# Revit family: PRD_AR_JntrlUnits_SiriusMultiPurposeSink_LTJ450,LTJ500
name_source: partatom
category: Plumbing Fixtures
revit_build: Autodesk Revit 2018 (Build: 20190510_1515(x64)
units: mm (PartAtom-declared; Revit-internal decimal feet)

## family parameters
Cut with Voids When Loaded = No
Host = Face
OmniClass Number = 23.45.05.14.14
OmniClass Title = Sinks/Lavatories
Part Type = Normal
Room Calculation Point = No
Round Connector Dimension = Use Diameter
Shared = No

## types (2) — shared parameters
AssetType = Fixed
Category = Pr_40_20_96_44, Janitorial sinks
Color = Stainless steel
Default Elevation = 850 mm  [stored 2.78871 ft]
DrainSize = DN 40 (1 1/2 inch.)
DurationUnit = year
Finish = Satin finished
FinishAndMaterial = Stainless steel 1.4301
Form = Stainless steel multi purpose sink
IfcExportAs = IfcSanitaryTerminalType
IfcExportType = SINK
IntegralAccessories = incl. stainless steel screws and dowels
Manufacturer = KWC Group AG
ManufacturerName = KWC Group AG
ManufacturerURL = www.kwc.com
Material = Stainless steel
NBSDescription = Janitorial units
NBSReference = 45-35-70/401
NominalHeight = 270 mm  [stored 0.885827 ft]
OutletSize = DN 40 (1 1/2 inch.)
ProductInformation = https://pim.kwc.com
Shape = Rectangular
SinkMaterial = PRD_AR_StainlessSteel_SatinFinished
SinkMounting = WallHung
SinkType = Other
URL = www.kwc.com
Uniclass2015Code = Pr_40_20_96_44
Uniclass2015Title = Janitorial sinks
Uniclass2015Version = Products v1.10
Version = 1
WarrantyDurationUnit = year
WasteSize = 40  [stored 0.131234 ft]
WaterSupplyOverflowAndWasteHolesOverflow = Yes
WaterSupplyOverflowAndWasteHolesWaste = Center-Center
WaterSupplyOverflowAndWasteHolesWaterSupply = No tapholes

## per-type parameters (varying)
| type | BIMObjectName | Description | Features | GrossWeight | HingedGrateZSIRX001 | ModelNumber | Name | NetWeight | NominalDepth | NominalWidth | Size |
| LTJ450 | PRD_AR_JanitorialUnits_SiriusMultiPurposeSink_LTJ450 | General purpose utility sink for wall mounting, stainless steel, surface satin finished, material thickness 0.9 mm, front panel with riffle, 1 1/2 centric plug waste, with overflow, 30 mm rear upstand, prewelded mounting brackets, incl. stainless steel screws and dowels. Optinally available hinged grid Z-SIRX001: loosely attached - for side mount. | stainless steel, 0.90 mm, satin finished, wall mounting, 470x270x430 mm (WxHxD) | 5.10 kg | Yes | 2000057085 | Sirius multi purpose sink LTJ450 | 4.40 kg | 430 mm  [stored 1.41076 ft] | 470 mm  [stored 1.54199 ft] | 470 x 430 x 270 mm |
| LTJ500 | PRD_AR_JanitorialUnits_SiriusMultiPurposeSink_LTJ500 | General purpose utility sink for wall mounting, stainless steel, surface satin finished, material thickness 0.9 mm, front panel with riffle, 1 1/2 centric plug waste, with overflow, 30 mm rear upstand, prewelded mounting brackets, incl. stainless steel screws and dowels. | stainless steel, 0.90 mm, satin finished, wall mounting, 520x270x490 mm (WxHxD) | 5.60 kg | No | 2000057087 | Sirius multi purpose sink LTJ500 | 4.90 kg | 490 mm  [stored 1.60761 ft] | 520 mm  [stored 1.70604 ft] | 520 x 490 x 270 mm |

note: column(s) folded — value = type name in every type: Model, ModelReference, TypeOfSink

note: [stored X ft] marks values corroborated as IEEE doubles in the binary element streams (Revit-internal decimal feet)

## geometry (parser evidence)
native form markers: Sweep x15
no freeform markers — native parametric forms only
